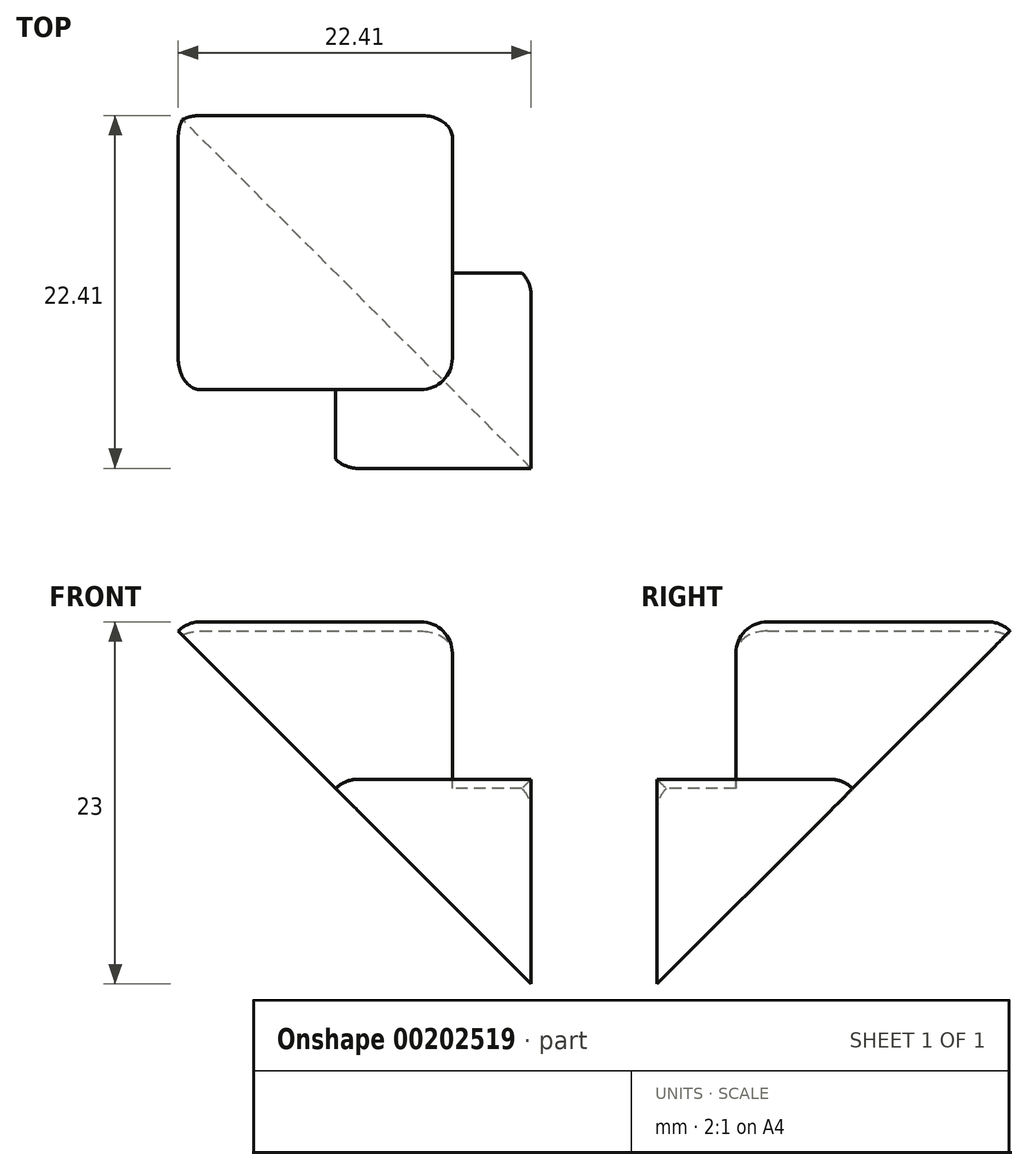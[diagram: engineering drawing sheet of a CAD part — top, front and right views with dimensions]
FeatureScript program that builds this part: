
annotation { "Feature Type Name" : "Feature", "Feature Type Description" : "" }
export const myFeature = defineFeature(function(context is Context, id is Id, definition is map)
    precondition{}
    {
        {
            var Q0;
            Q0=qCreatedBy(makeId("Front.planeOp"),FACE);
            var sketch = newSketch(context, id + "F0", { "sketchPlane" : qUnion([Q0])});
            skLineSegment(sketch, "E0.bottom", {"start": v(0, 0) * mm, "end": v(-18, 0) * mm});
            skLineSegment(sketch, "E0.top", {"start": v(0, 18) * mm, "end": v(-18, 18) * mm});
            skLineSegment(sketch, "E0.left", {"start": v(0, 0) * mm, "end": v(0, 18) * mm});
            skLineSegment(sketch, "E0.right", {"start": v(-18, 0) * mm, "end": v(-18, 18) * mm});
            skSolve(sketch);
        }
        {
            var Q0;
            Q0 = qSketchRegion(id + "F0", true);
            extrude(context, id + "F1", {"entities" : qUnion([Q0]), "oppositeDirection" : true, "depth" : 18 * mm});
        }
        {
            var Q0;
            Q0=qCreatedBy(makeId("Top.planeOp"),FACE);
            var sketch = newSketch(context, id + "F2", { "sketchPlane" : qUnion([Q0])});
            skLineSegment(sketch, "E1.bottom", {"start": v(5, -5) * mm, "end": v(-5, -5) * mm});
            skLineSegment(sketch, "E1.top", {"start": v(5, 5) * mm, "end": v(-5, 5) * mm});
            skLineSegment(sketch, "E1.left", {"start": v(5, -5) * mm, "end": v(5, 5) * mm});
            skLineSegment(sketch, "E1.right", {"start": v(-5, -5) * mm, "end": v(-5, 5) * mm});
            skPoint(sketch, "E1.middle", {"position": v(0, 0) * mm});
            skLineSegment(sketch, "E2", {"start": v(-5, 5) * mm, "end": v(-8, 5) * mm});
            skLineSegment(sketch, "E3", {"start": v(-8, 5) * mm, "end": v(-8, 8) * mm});
            skLineSegment(sketch, "E4", {"start": v(-8, 8) * mm, "end": v(-5, 8) * mm});
            skLineSegment(sketch, "E5", {"start": v(-5, 8) * mm, "end": v(-5, 5) * mm});
            skLineSegment(sketch, "E6.bottom", {"start": v(-8, 8) * mm, "end": v(5, 8) * mm});
            skLineSegment(sketch, "E6.top", {"start": v(-8, -5) * mm, "end": v(5, -5) * mm});
            skLineSegment(sketch, "E6.left", {"start": v(-8, 8) * mm, "end": v(-8, -5) * mm});
            skLineSegment(sketch, "E6.right", {"start": v(5, 8) * mm, "end": v(5, -5) * mm});
            skSolve(sketch);
        }
        {
            var Q0;
            Q0 = qSketchRegion(id + "F2", true);
            extrude(context, id + "F3", {"entities" : qUnion([Q0]), "operationType" : NewBodyOperationType.ADD, "oppositeDirection" : true, "depth" : 5 * mm});
        }
        {
            var Q0;
            Q0 = qSketchRegion(id + "F2", true);
            extrude(context, id + "F4", {"entities" : qUnion([Q0]), "operationType" : NewBodyOperationType.ADD, "depth" : 8 * mm});
        }
        {
            var Q0;
            Q0=makeQuery(id+"F1.opExtrude","CAP_EDGE",EDGE,{"disambiguationData":[OSD([sQuery(id+"F0.wireOp",EDGE,"E0.right")])],"isStart":false});
            var Q1;
            Q1=makeQuery(id+"F1.opExtrude","SWEPT_EDGE",EDGE,{"disambiguationData":[OSD([sQuery(id+"F0.wireOp",EDGE,"E0.top"),sQuery(id+"F0.wireOp",EDGE,"E0.right")])]});
            var Q2;
            Q2=makeQuery(id+"F1.opExtrude","CAP_EDGE",EDGE,{"disambiguationData":[OSD([sQuery(id+"F0.wireOp",EDGE,"E0.top")])],"isStart":false});
            fillet(context, id + "F5", {"entities" : qUnion([Q0, Q1, Q2]), "radius" : 2 * mm, "tangentPropagation" : true, "allowEdgeOverflow" : false});
        }
        {
            var Q0;
            Q0=makeQuery(id+"F1.opExtrude","SWEPT_EDGE",EDGE,{"disambiguationData":[OSD([sQuery(id+"F0.wireOp",EDGE,"E0.top"),sQuery(id+"F0.wireOp",EDGE,"E0.left")])]});
            var Q1;
            Q1=makeQuery(id+"F1.opExtrude","CAP_EDGE",EDGE,{"disambiguationData":[OSD([sQuery(id+"F0.wireOp",EDGE,"E0.top")])],"isStart":true});
            var Q2;
            Q2=makeQuery(id+"F1.opExtrude","SWEPT_EDGE",EDGE,{"disambiguationData":[OSD([sQuery(id+"F0.wireOp",EDGE,"E0.bottom"),sQuery(id+"F0.wireOp",EDGE,"E0.right")])]});
            fillet(context, id + "F6", {"entities" : qUnion([Q0, Q1, Q2]), "radius" : 2 * mm, "tangentPropagation" : true, "allowEdgeOverflow" : false});
        }
        {
            var Q0;
            {var subQ0=sQuery(id+"F0.wireOp",EDGE,"E0.left");var subQ2=sQuery(id+"F0.wireOp",EDGE,"E0.bottom");Q0=makeQuery(id+"F3.boolean.opBoolean","SPLIT",EDGE,{"disambiguationData":[TD([makeQuery(id+"F1.opExtrude","CAP_FACE",FACE,{"disambiguationData":[OSD([subQ2,sQuery(id+"F0.wireOp",EDGE,"E0.top"),subQ0,sQuery(id+"F0.wireOp",EDGE,"E0.right")])],"isStart":false})])],"derivedFrom":makeQuery(id+"F1.opExtrude","SWEPT_EDGE",EDGE,{"disambiguationData":[OSD([subQ2,subQ0])]})});}
            var Q1;
            Q1=makeQuery(id+"F1.opExtrude","CAP_EDGE",EDGE,{"disambiguationData":[OSD([sQuery(id+"F0.wireOp",EDGE,"E0.left")])],"isStart":true});
            var Q2;
            {var subQ0=sQuery(id+"F0.wireOp",EDGE,"E0.right");var subQ2=sQuery(id+"F0.wireOp",EDGE,"E0.bottom");Q2=makeQuery(id+"F3.boolean.opBoolean","SPLIT",EDGE,{"disambiguationData":[TD([makeQuery(id+"F1.opExtrude","SWEPT_FACE",FACE,{"disambiguationData":[OSD([subQ0])]})])],"derivedFrom":makeQuery(id+"F1.opExtrude","CAP_EDGE",EDGE,{"disambiguationData":[OSD([subQ2])],"isStart":true})});}
            fillet(context, id + "F7", {"entities" : qUnion([Q0, Q1, Q2]), "radius" : 2 * mm, "tangentPropagation" : true, "allowEdgeOverflow" : false});
        }
        {
            var Q0;
            Q0=makeQuery(id+"F4.opExtrude","CAP_EDGE",EDGE,{"disambiguationData":[OSD([sQuery(id+"F2.wireOp",EDGE,"E6.left")])],"isStart":false});
            var Q1;
            Q1=makeQuery(id+"F4.opExtrude","CAP_EDGE",EDGE,{"disambiguationData":[OSD([sQuery(id+"F2.wireOp",EDGE,"E6.bottom")])],"isStart":false});
            var Q2;
            Q2=makeQuery(id+"F3.opExtrude","SWEPT_EDGE",EDGE,{"disambiguationData":[OSD([sQuery(id+"F2.wireOp",EDGE,"E6.bottom"),sQuery(id+"F2.wireOp",EDGE,"E6.left")])]});
            fillet(context, id + "F8", {"entities" : qUnion([Q0, Q1, Q2]), "radius" : 2 * mm, "tangentPropagation" : true, "allowEdgeOverflow" : false});
        }
        {
            var Q0;
            Q0=qCreatedBy(makeId("Front.planeOp"),FACE);
            var sketch = newSketch(context, id + "F9", { "sketchPlane" : qUnion([Q0])});
            skLineSegment(sketch, "E7", {"start": v(-18, 18) * mm, "end": v(5, -5) * mm});
            skLineSegment(sketch, "E8", {"start": v(5, -5) * mm, "end": v(-18, -5) * mm});
            skLineSegment(sketch, "E9", {"start": v(-18, -5) * mm, "end": v(-18, 18) * mm});
            skSolve(sketch);
        }
        {
            var Q0;
            Q0=makeQuery(id+"F9.imprint","IMPRINT",FACE,{"disambiguationData":[TD([[makeQuery(id+"F9.imprint","IMPRINT",EDGE,{"derivedFrom":sQuery(id+"F9.wireOp",EDGE,"E7")}),-1.0]])]});
            extrude(context, id + "F10", {"entities" : qUnion([Q0]), "operationType" : NewBodyOperationType.REMOVE, "depth" : 40 * mm, "symmetric" : true});
        }
        {
            var Q0;
            Q0=qCreatedBy(makeId("Right.planeOp"),FACE);
            var sketch = newSketch(context, id + "F11", { "sketchPlane" : qUnion([Q0])});
            skLineSegment(sketch, "E10", {"start": v(-5, -5) * mm, "end": v(18, 18) * mm});
            skLineSegment(sketch, "E11", {"start": v(18, 18) * mm, "end": v(18, -5) * mm});
            skLineSegment(sketch, "E12", {"start": v(18, -5) * mm, "end": v(-5, -5) * mm});
            skSolve(sketch);
        }
        {
            var Q0;
            Q0 = qSketchRegion(id + "F11", true);
            extrude(context, id + "F12", {"entities" : qUnion([Q0]), "operationType" : NewBodyOperationType.REMOVE, "oppositeDirection" : true, "depth" : 40 * mm, "symmetric" : true});
        }
    });
